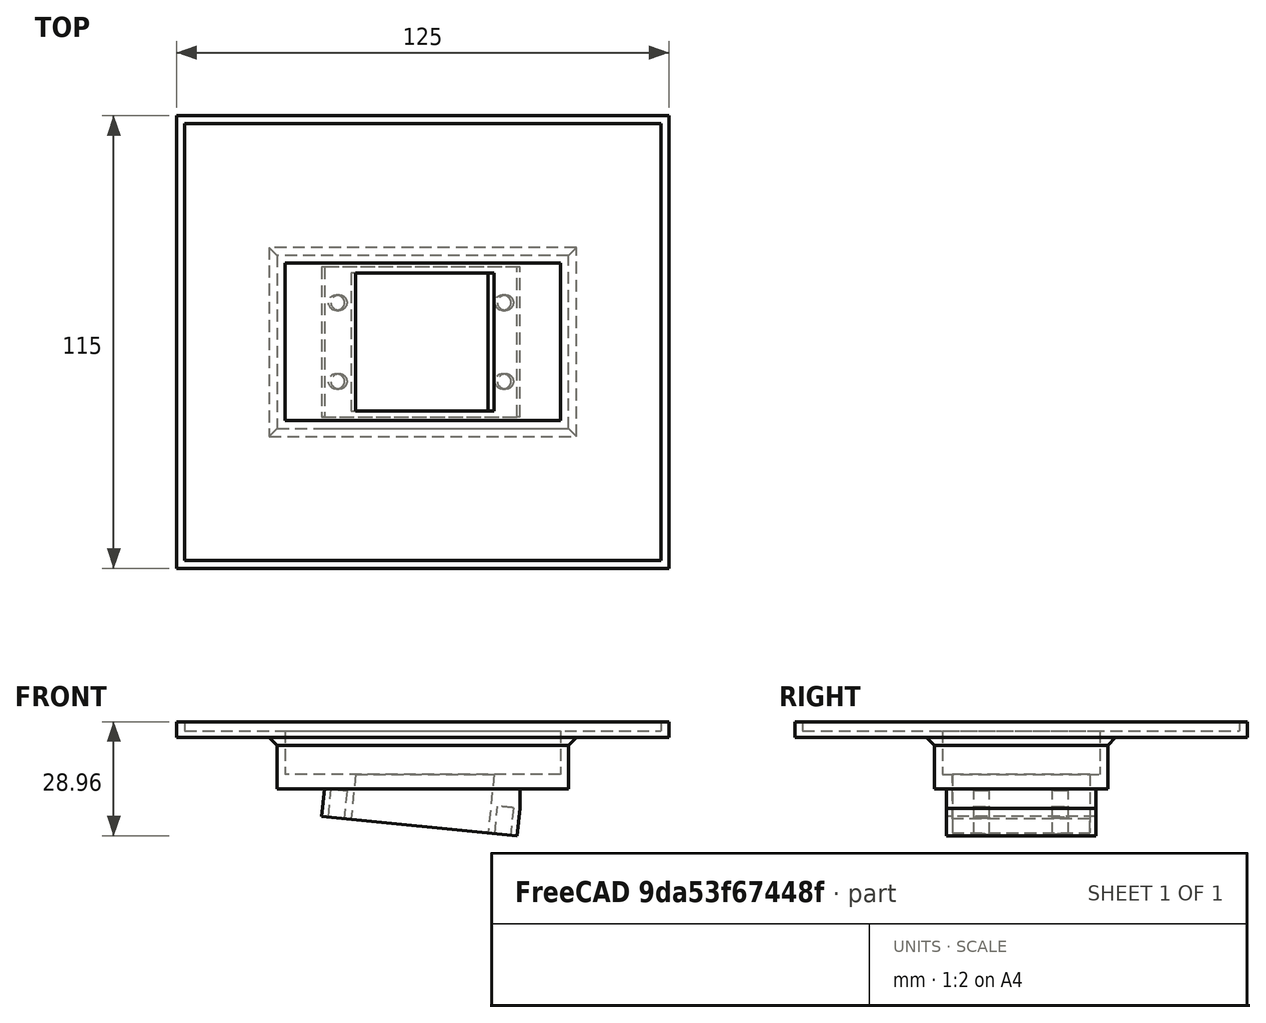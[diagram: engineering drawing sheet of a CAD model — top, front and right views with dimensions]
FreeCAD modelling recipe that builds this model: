
FCSTD DOCUMENT  (FreeCAD 0.18R4 (GitTag))
Label: SolarPanelHolder
License: All rights reserved
LicenseURL: http://en.wikipedia.org/wiki/All_rights_reserved
objects: TechDraw::DrawViewDimension×18, Sketcher::SketchObject×8, PartDesign::Pad×4, PartDesign::Pocket×4, TechDraw::DrawProjGroupItem×3, TechDraw::DrawSVGTemplate×2, TechDraw::DrawPage×2, PartDesign::Chamfer×1, PartDesign::Body×1, TechDraw::DrawViewPart×1, TechDraw::DrawProjGroup×1
note: 26 computed .brp shape members not serialized (recipe doc carries the construction recipe); baked Part::Feature solids carry a one-line shape summary decoded from their .brp

FEATURE [Sketcher::SketchObject] Sketch
  MapMode = 5
  Support = -> [XY_Plane]
  sketch-geometry (4):
    g0: LineSegment StartX=0 StartY=0 StartZ=0 EndX=125 EndY=0 EndZ=0
    g1: LineSegment StartX=125 StartY=0 StartZ=0 EndX=125 EndY=115 EndZ=0
    g2: LineSegment StartX=125 StartY=115 StartZ=0 EndX=0 EndY=115 EndZ=0
    g3: LineSegment StartX=0 StartY=115 StartZ=0 EndX=0 EndY=0 EndZ=0
  constraints (11):
    c: Coincident(g0,g1)
    c: Coincident(g1,g2)
    c: Coincident(g2,g3)
    c: Coincident(g3,g0)
    c: Horizontal(g0)
    c: Horizontal(g2)
    c: Vertical(g1)
    c: Vertical(g3)
    c: Coincident(g0,g-1)
    c: DistanceX(g2,g2) = 125
    c: DistanceY(g1,g1) = 115
FEATURE [PartDesign::Pad] Pad
  Length = 4
  Length2 = 100
  Profile = -> Sketch
  Refine = true
  Type = 0
FEATURE [Sketcher::SketchObject] Sketch001
  MapMode = 5
  Placement = pos=(0,0,4) rot=(0,0,1;0rad)
  Support = -> [Pad]
  sketch-geometry (4):
    g0: LineSegment StartX=2 StartY=2 StartZ=0 EndX=123 EndY=2 EndZ=0
    g1: LineSegment StartX=123 StartY=2 StartZ=0 EndX=123 EndY=113 EndZ=0
    g2: LineSegment StartX=123 StartY=113 StartZ=0 EndX=2 EndY=113 EndZ=0
    g3: LineSegment StartX=2 StartY=113 StartZ=0 EndX=2 EndY=2 EndZ=0
  constraints (12):
    c: Coincident(g0,g1)
    c: Coincident(g1,g2)
    c: Coincident(g2,g3)
    c: Coincident(g3,g0)
    c: Horizontal(g0)
    c: Horizontal(g2)
    c: Vertical(g1)
    c: Vertical(g3)
    c: DistanceX(g-1,g0) = 2
    c: DistanceY(g-1,g0) = 2
    c: DistanceY(g3,g3) = 111
    c: DistanceX(g2,g2) = 121
FEATURE [PartDesign::Pocket] Pocket
  BaseFeature = -> Pad
  Length = 2.3
  Length2 = 100
  Profile = -> Sketch001
  Refine = true
  Type = 0
FEATURE [Sketcher::SketchObject] Sketch002
  ExternalGeometry = -> [Pocket]
  MapMode = 5
  Placement = pos=(0,0,0) rot=(1,0,0;3.14159rad)
  Support = -> [Pocket]
  sketch-geometry (4):
    g0: LineSegment StartX=25.5 StartY=-35.5 StartZ=0 EndX=99.5 EndY=-35.5 EndZ=0
    g1: LineSegment StartX=99.5 StartY=-35.5 StartZ=0 EndX=99.5 EndY=-79.5 EndZ=0
    g2: LineSegment StartX=99.5 StartY=-79.5 StartZ=0 EndX=25.5 EndY=-79.5 EndZ=0
    g3: LineSegment StartX=25.5 StartY=-79.5 StartZ=0 EndX=25.5 EndY=-35.5 EndZ=0
  constraints (12):
    c: Coincident(g0,g1)
    c: Coincident(g1,g2)
    c: Coincident(g2,g3)
    c: Coincident(g3,g0)
    c: Horizontal(g0)
    c: Horizontal(g2)
    c: Vertical(g1)
    c: Vertical(g3)
    c: DistanceX(g-1,g0) = 25.5
    c: DistanceY(g0,g-1) = 35.5
    c: DistanceY(g-6,g2) = 35.5
    c: DistanceX(g0,g-4) = 25.5
FEATURE [PartDesign::Pad] Pad001
  BaseFeature = -> Pocket
  Length = 13
  Length2 = 100
  Profile = -> Sketch002
  Refine = true
  Type = 0
FEATURE [PartDesign::Chamfer] Chamfer
  Base = -> Pad001 [Edge12,Edge13,Edge14,Edge15]
  BaseFeature = -> Pad001
  Size = 2
FEATURE [Sketcher::SketchObject] Sketch003
  ExternalGeometry = -> [Chamfer]
  MapMode = 5
  Placement = pos=(0,0,1.7) rot=(0,0,1;0rad)
  Support = -> [Chamfer]
  sketch-geometry (4):
    g0: LineSegment StartX=27.5 StartY=77.5 StartZ=0 EndX=97.5 EndY=77.5 EndZ=0
    g1: LineSegment StartX=97.5 StartY=77.5 StartZ=0 EndX=97.5 EndY=37.5 EndZ=0
    g2: LineSegment StartX=97.5 StartY=37.5 StartZ=0 EndX=27.5 EndY=37.5 EndZ=0
    g3: LineSegment StartX=27.5 StartY=37.5 StartZ=0 EndX=27.5 EndY=77.5 EndZ=0
  constraints (12):
    c: Coincident(g0,g1)
    c: Coincident(g1,g2)
    c: Coincident(g2,g3)
    c: Coincident(g3,g0)
    c: Horizontal(g0)
    c: Horizontal(g2)
    c: Vertical(g1)
    c: Vertical(g3)
    c: DistanceX(g-6,g2) = 25.5
    c: DistanceX(g1,g-5) = 25.5
    c: DistanceY(g0,g-6) = 35.5
    c: DistanceY(g-6,g2) = 35.5
FEATURE [PartDesign::Pocket] Pocket001
  BaseFeature = -> Chamfer
  Length = 11
  Length2 = 100
  Profile = -> Sketch003
  Refine = true
  Type = 0
FEATURE [Sketcher::SketchObject] Sketch004
  ExternalGeometry = -> [Pocket001]
  MapMode = 5
  Placement = pos=(0,0,-13) rot=(1,0,0;3.14159rad)
  Support = -> [Pocket001]
  sketch-geometry (4):
    g0: LineSegment StartX=37.5 StartY=-38.5 StartZ=0 EndX=87.2 EndY=-38.5 EndZ=0
    g1: LineSegment StartX=87.2 StartY=-38.5 StartZ=0 EndX=87.2 EndY=-76.5 EndZ=0
    g2: LineSegment StartX=87.2 StartY=-76.5 StartZ=0 EndX=37.5 EndY=-76.5 EndZ=0
    g3: LineSegment StartX=37.5 StartY=-76.5 StartZ=0 EndX=37.5 EndY=-38.5 EndZ=0
  constraints (12):
    c: Coincident(g0,g1)
    c: Coincident(g1,g2)
    c: Coincident(g2,g3)
    c: Coincident(g3,g0)
    c: Horizontal(g0)
    c: Horizontal(g2)
    c: Vertical(g1)
    c: Vertical(g3)
    c: DistanceX(g0,g0) = 49.7
    c: DistanceY(g3,g3) = 38
    c: DistanceY(g0,g-6) = 3
    c: DistanceX(g-6,g0) = 12
FEATURE [PartDesign::Pad] Pad002
  BaseFeature = -> Pocket001
  Length = 5
  Length2 = 100
  Profile = -> Sketch004
  Refine = true
  Type = 0
FEATURE [Sketcher::SketchObject] Sketch005
  ExternalGeometry = -> [Pad002]
  MapMode = 5
  Placement = pos=(0,76.5,0) rot=(0,0.707107,0.707107;3.14159rad)
  Support = -> [Pad002]
  sketch-geometry (3):
    g0: LineSegment StartX=-37.5 StartY=-13 StartZ=0 EndX=-87.2 EndY=-18 EndZ=0
    g1: LineSegment StartX=-87.2 StartY=-18 StartZ=0 EndX=-37.5 EndY=-18 EndZ=0
    g2: LineSegment StartX=-37.5 StartY=-18 StartZ=0 EndX=-37.5 EndY=-13 EndZ=0
  constraints (6):
    c: Coincident(g-3,g0)
    c: Coincident(g0,g-4)
    c: Coincident(g0,g1)
    c: Coincident(g1,g-4)
    c: Coincident(g1,g2)
    c: Coincident(g2,g0)
FEATURE [PartDesign::Pocket] Pocket002
  BaseFeature = -> Pad002
  Length = 5
  Length2 = 100
  Profile = -> Sketch005
  Refine = true
  Type = 1
FEATURE [Sketcher::SketchObject] Sketch006
  ExternalGeometry = -> [Pocket002]
  MapMode = 5
  Placement = pos=(-0.919005,-2e-15,-9.13491) rot=(0.998744,0,-0.050112;3.14159rad)
  Support = -> [Pocket002]
  sketch-geometry (12):
    g0: LineSegment StartX=38.6129 StartY=-38.5 StartZ=0 EndX=88.5638 EndY=-38.5 EndZ=0
    g1: LineSegment StartX=88.5638 StartY=-38.5 StartZ=0 EndX=88.5638 EndY=-76.5 EndZ=0
    g2: LineSegment StartX=88.5638 StartY=-76.5 StartZ=0 EndX=38.6129 EndY=-76.5 EndZ=0
    g3: LineSegment StartX=38.6129 StartY=-76.5 StartZ=0 EndX=38.6129 EndY=-38.5 EndZ=0
    g4: LineSegment StartX=46.1129 StartY=-40 StartZ=0 EndX=81.1129 EndY=-40 EndZ=0
    g5: LineSegment StartX=81.1129 StartY=-40 StartZ=0 EndX=81.1129 EndY=-75 EndZ=0
    g6: LineSegment StartX=81.1129 StartY=-75 StartZ=0 EndX=46.1129 EndY=-75 EndZ=0
    g7: LineSegment StartX=46.1129 StartY=-75 StartZ=0 EndX=46.1129 EndY=-40 EndZ=0
    g8: Circle CenterX=42.3629 CenterY=-47.5 CenterZ=0 NormalX=0 NormalY=0 NormalZ=1 AngleXU=0 Radius=2
    g9: Circle CenterX=42.3629 CenterY=-67.5 CenterZ=0 NormalX=0 NormalY=0 NormalZ=1 AngleXU=0 Radius=2
    g10: Circle CenterX=84.8629 CenterY=-47.5 CenterZ=0 NormalX=0 NormalY=0 NormalZ=1 AngleXU=0 Radius=2
    g11: Circle CenterX=84.8629 CenterY=-67.5 CenterZ=0 NormalX=0 NormalY=0 NormalZ=1 AngleXU=0 Radius=2
  constraints (34):
    c: Coincident(g0,g1)
    c: Coincident(g1,g2)
    c: Coincident(g2,g3)
    c: Coincident(g3,g0)
    c: Horizontal(g0)
    c: Horizontal(g2)
    c: Vertical(g1)
    c: Vertical(g3)
    c: Coincident(g0,g-6)
    c: Coincident(g1,g-5)
    c: Coincident(g4,g5)
    c: Coincident(g5,g6)
    c: Coincident(g6,g7)
    c: Coincident(g7,g4)
    c: Horizontal(g4)
    c: Horizontal(g6)
    c: Vertical(g5)
    c: Vertical(g7)
    c: DistanceX(g4,g4) = 35
    c: DistanceY(g5,g5) = 35
    c: DistanceY(g4,g0) = 1.5
    c: DistanceX(g0,g4) = 7.5
    c: Diameter(g8) = 4
    c: Equal(g8,g9)
    c: Equal(g8,g10)
    c: Equal(g8,g11)
    c: DistanceY(g9,g8) = 20
    c: DistanceY(g11,g10) = 20
    c: DistanceY(g8,g0) = 9
    c: DistanceY(g10,g0) = 9
    c: DistanceX(g0,g8) = 3.75
    c: DistanceX(g0,g9) = 3.75
    c: DistanceX(g0,g10) = 46.25
    c: DistanceX(g0,g11) = 46.25
FEATURE [PartDesign::Pad] Pad003
  BaseFeature = -> Pocket002
  Length = 7
  Length2 = 100
  Profile = -> Sketch006
  Refine = true
  Type = 0
FEATURE [Sketcher::SketchObject] Sketch007
  ExternalGeometry = -> [Pad003]
  MapMode = 5
  Placement = pos=(-0.919005,-2e-15,-9.13491) rot=(0.998744,0,-0.050112;3.14159rad)
  Support = -> [Pad003]
  sketch-geometry (4):
    g0: LineSegment StartX=46.1129 StartY=-40 StartZ=0 EndX=81.1129 EndY=-40 EndZ=0
    g1: LineSegment StartX=81.1129 StartY=-40 StartZ=0 EndX=81.1129 EndY=-75 EndZ=0
    g2: LineSegment StartX=81.1129 StartY=-75 StartZ=0 EndX=46.1129 EndY=-75 EndZ=0
    g3: LineSegment StartX=46.1129 StartY=-75 StartZ=0 EndX=46.1129 EndY=-40 EndZ=0
  constraints (10):
    c: Coincident(g0,g1)
    c: Coincident(g1,g2)
    c: Coincident(g2,g3)
    c: Coincident(g3,g0)
    c: Horizontal(g0)
    c: Horizontal(g2)
    c: Vertical(g1)
    c: Vertical(g3)
    c: Coincident(g0,g-3)
    c: Coincident(g1,g-4)
FEATURE [PartDesign::Pocket] Pocket003
  BaseFeature = -> Pad003
  Length = 5
  Length2 = 100
  Profile = -> Sketch007
  Refine = true
  Type = 1
FEATURE [PartDesign::Body] Body
  Group = -> [Sketch,Pad,Sketch001,Pocket,Sketch002,Pad001,Chamfer,Sketch003,Pocket001,Sketch004,Pad002,Sketch005,Pocket002,Sketch006,Pad003,Sketch007,Pocket003]
  Origin = -> Origin
  Tip = -> Pocket003
FEATURE [TechDraw::DrawSVGTemplate] Template
  EditableTexts = APPROVER_NAME=APPROVER NAME; AUTHOR_NAME=AUTHOR NAME; DATE=YYYY-MM-DD; DN=DN; OWNER_NAME=OWNER NAME; PM=PM; PN=PN; REVISION=REV A; RIGHTS=(R) DO NOT DUPLICATE THIS DRAWING TO THIRD PARTIES WITHOUT OWNER'S PERMISSION !; SCALE=M x:x; SHEET=99 of 99; SIZE=A4; TITLELINE-1=FreeCAD; TOLERANCE=+/- ?
  Height = 210
  Orientation = 1
  Width = 297
FEATURE [TechDraw::DrawViewPart] View
  CoarseView = false
  Direction = (0.507,0.24,-0.828)
  Focus = 100
  HardHidden = false
  IsoCount = 0
  IsoHidden = false
  IsoVisible = false
  LockPosition = false
  Perspective = false
  Rotation = 0
  ScaleType = 0
  SeamHidden = false
  SeamVisible = false
  SmoothHidden = false
  SmoothVisible = false
  Source = -> [Body]
  X = 130.85
  Y = 119.408
FEATURE [TechDraw::DrawPage] Page
  KeepUpdated = true
  ProjectionType = 0
  Template = -> Template
  Views = -> [View]
FEATURE [TechDraw::DrawSVGTemplate] Template001
  EditableTexts = APPROVER_NAME=APPROVER NAME; AUTHOR_NAME=AUTHOR NAME; DATE=YYYY-MM-DD; DN=DN; OWNER_NAME=OWNER NAME; PM=PM; PN=PN; REVISION=REV A; RIGHTS=(R) DO NOT DUPLICATE THIS DRAWING TO THIRD PARTIES WITHOUT OWNER'S PERMISSION !; SCALE=M x:x; SHEET=99 of 99; SIZE=A4; TITLELINE-1=FreeCAD; TOLERANCE=+/- ?
  Height = 210
  Orientation = 1
  Width = 297
FEATURE [TechDraw::DrawProjGroupItem] ProjItem  label="Front"
  CoarseView = false
  Direction = (0,0,1)
  Focus = 100
  HardHidden = false
  IsoCount = 0
  IsoHidden = false
  IsoVisible = false
  LockPosition = true
  Perspective = false
  Rotation = 0
  RotationVector = (0,1,0)
  Scale = 0.5
  ScaleType = 2
  SeamHidden = false
  SeamVisible = false
  SmoothHidden = false
  SmoothVisible = false
  Source = -> [Body]
  Type = 0
  X = 0
  Y = 0
FEATURE [TechDraw::DrawProjGroupItem] ProjItem001  label="Right"
  CoarseView = false
  Direction = (0,1,1e-16)
  Focus = 100
  HardHidden = false
  IsoCount = 0
  IsoHidden = false
  IsoVisible = false
  LockPosition = false
  Perspective = false
  Rotation = 0
  RotationVector = (0,1e-16,-1)
  Scale = 0.5
  ScaleType = 2
  SeamHidden = false
  SeamVisible = false
  SmoothHidden = false
  SmoothVisible = false
  Source = -> [Body]
  Type = 2
  X = -87.5
  Y = 0
FEATURE [TechDraw::DrawProjGroupItem] ProjItem002  label="Rear"
  CoarseView = false
  Direction = (0,1e-16,-1)
  Focus = 100
  HardHidden = false
  IsoCount = 0
  IsoHidden = false
  IsoVisible = false
  LockPosition = false
  Perspective = false
  Rotation = 0
  RotationVector = (0,-1,0)
  Scale = 0.5
  ScaleType = 2
  SeamHidden = false
  SeamVisible = false
  SmoothHidden = false
  SmoothVisible = false
  Source = -> [Body]
  Type = 3
  X = 87.5
  Y = 0
FEATURE [TechDraw::DrawProjGroup] ProjGroup
  Anchor = -> ProjItem
  AutoDistribute = true
  LockPosition = false
  ProjectionType = 0
  Rotation = 0
  Scale = 0.5
  ScaleType = 0
  Source = -> [Body]
  Views = -> [ProjItem,ProjItem001,ProjItem002]
  X = 135.354
  Y = 105.811
  spacingX = 30
  spacingY = 15
FEATURE [TechDraw::DrawViewDimension] Dimension
  Arbitrary = false
  FormatSpec = %.2f
  LockPosition = false
  MeasureType = 1
  OverTolerance = 0
  References2D = -> [ProjItem]
  Rotation = 0
  ScaleType = 0
  Type = 1
  UnderTolerance = 0
  X = -0.406504
  Y = 56.4002
FEATURE [TechDraw::DrawViewDimension] Dimension001
  Arbitrary = false
  FormatSpec = %.2f
  LockPosition = false
  MeasureType = 1
  OverTolerance = 0
  References2D = -> [ProjItem]
  Rotation = 0
  ScaleType = 0
  Type = 2
  UnderTolerance = 0
  X = -57.5702
  Y = -0.411015
FEATURE [TechDraw::DrawViewDimension] Dimension002
  Arbitrary = false
  FormatSpec = %.2f
  LockPosition = false
  MeasureType = 1
  OverTolerance = 0
  References2D = -> [ProjItem]
  Rotation = 0
  ScaleType = 0
  Type = 1
  UnderTolerance = 0
  X = -0.532813
  Y = 48.846
FEATURE [TechDraw::DrawViewDimension] Dimension003
  Arbitrary = false
  FormatSpec = %.2f
  LockPosition = false
  MeasureType = 1
  OverTolerance = 0
  References2D = -> [ProjItem]
  Rotation = 0
  ScaleType = 0
  Type = 2
  UnderTolerance = 0
  X = -48.2486
  Y = -0.920818
FEATURE [TechDraw::DrawViewDimension] Dimension004
  Arbitrary = false
  FormatSpec = %.2f
  LockPosition = false
  MeasureType = 1
  OverTolerance = 0
  References2D = -> [ProjItem002]
  Rotation = 0
  ScaleType = 0
  Type = 1
  UnderTolerance = 0
  X = 1.04211
  Y = 50.6062
FEATURE [TechDraw::DrawViewDimension] Dimension005
  Arbitrary = false
  FormatSpec = %.2f
  LockPosition = false
  MeasureType = 1
  OverTolerance = 0
  References2D = -> [ProjItem002]
  Rotation = 0
  ScaleType = 0
  Type = 1
  UnderTolerance = 0
  X = 1.51784
  Y = 40.8336
FEATURE [TechDraw::DrawViewDimension] Dimension006
  Arbitrary = false
  FormatSpec = %.2f
  LockPosition = false
  MeasureType = 1
  OverTolerance = 0
  References2D = -> [ProjItem002]
  Rotation = 0
  ScaleType = 0
  Type = 2
  UnderTolerance = 0
  X = 43.7018
  Y = -0.156532
FEATURE [TechDraw::DrawViewDimension] Dimension007
  Arbitrary = false
  FormatSpec = %.2f
  LockPosition = false
  MeasureType = 1
  OverTolerance = 0
  References2D = -> [ProjItem002]
  Rotation = 0
  ScaleType = 0
  Type = 2
  UnderTolerance = 0
  X = 33.0509
  Y = 0.795492
FEATURE [TechDraw::DrawViewDimension] Dimension008
  Arbitrary = false
  FormatSpec = %.2f
  LockPosition = false
  MeasureType = 1
  OverTolerance = 0
  References2D = -> [ProjItem002]
  Rotation = 0
  ScaleType = 0
  Type = 1
  UnderTolerance = 0
  X = 1.12923
  Y = -38.8471
FEATURE [TechDraw::DrawViewDimension] Dimension009
  Arbitrary = false
  FormatSpec = %.2f
  LockPosition = false
  MeasureType = 1
  OverTolerance = 0
  References2D = -> [ProjItem002]
  Rotation = 0
  ScaleType = 0
  Type = 2
  UnderTolerance = 0
  X = 33.4117
  Y = -26.7903
FEATURE [TechDraw::DrawViewDimension] Dimension010
  Arbitrary = false
  FormatSpec = %.2f
  LockPosition = false
  MeasureType = 1
  OverTolerance = 0
  References2D = -> [ProjItem001]
  Rotation = 0
  ScaleType = 0
  Type = 1
  UnderTolerance = 0
  X = -20.5468
  Y = 37.8754
FEATURE [TechDraw::DrawViewDimension] Dimension011
  Arbitrary = false
  FormatSpec = %.2f
  LockPosition = false
  MeasureType = 1
  OverTolerance = 0
  References2D = -> [ProjItem001]
  Rotation = 0
  ScaleType = 0
  Type = 1
  UnderTolerance = 0
  X = -18.2607
  Y = 46.0172
FEATURE [TechDraw::DrawViewDimension] Dimension012
  Arbitrary = false
  FormatSpec = %.2f
  LockPosition = false
  MeasureType = 1
  OverTolerance = 0
  References2D = -> [ProjItem001]
  Rotation = 0
  ScaleType = 0
  Type = 1
  UnderTolerance = 0
  X = -19.0553
  Y = 53.318
FEATURE [TechDraw::DrawViewDimension] Dimension013
  Arbitrary = false
  FormatSpec = %.2f
  LockPosition = false
  MeasureType = 1
  OverTolerance = 0
  References2D = -> [ProjItem001]
  Rotation = 0
  ScaleType = 0
  Type = 1
  UnderTolerance = 0
  X = -18.4581
  Y = 61.1938
FEATURE [TechDraw::DrawViewDimension] Dimension014
  Arbitrary = false
  FormatSpec = %.2f
  LockPosition = false
  MeasureType = 1
  OverTolerance = 0
  References2D = -> [ProjItem]
  Rotation = 0
  ScaleType = 0
  Type = 1
  UnderTolerance = 0
  X = -0.411115
  Y = 65.4304
FEATURE [TechDraw::DrawViewDimension] Dimension015
  Arbitrary = false
  FormatSpec = %.2f
  LockPosition = false
  MeasureType = 1
  OverTolerance = 0
  References2D = -> [ProjItem]
  Rotation = 0
  ScaleType = 0
  Type = 2
  UnderTolerance = 0
  X = 38.1572
  Y = 0.240975
FEATURE [TechDraw::DrawViewDimension] Dimension016
  Arbitrary = false
  FormatSpec = %.2f
  LockPosition = false
  MeasureType = 1
  OverTolerance = 0
  References2D = -> [ProjItem]
  Rotation = 0
  ScaleType = 0
  Type = 1
  UnderTolerance = 0
  X = 0.589032
  Y = 41.3933
FEATURE [TechDraw::DrawViewDimension] Dimension017
  Arbitrary = false
  FormatSpec = %.2f
  LockPosition = false
  MeasureType = 1
  OverTolerance = 0
  References2D = -> [ProjItem]
  Rotation = 0
  ScaleType = 0
  Type = 2
  UnderTolerance = 0
  X = -38.7656
  Y = 1.6957
FEATURE [TechDraw::DrawPage] Page001
  KeepUpdated = true
  ProjectionType = 0
  Template = -> Template001
  Views = -> [ProjGroup,Dimension,Dimension001,Dimension002,Dimension003,Dimension004,Dimension005,Dimension006,Dimension007,Dimension008,Dimension009,Dimension010,Dimension011,Dimension012,Dimension013,Dimension014,Dimension015,Dimension016,Dimension017]
